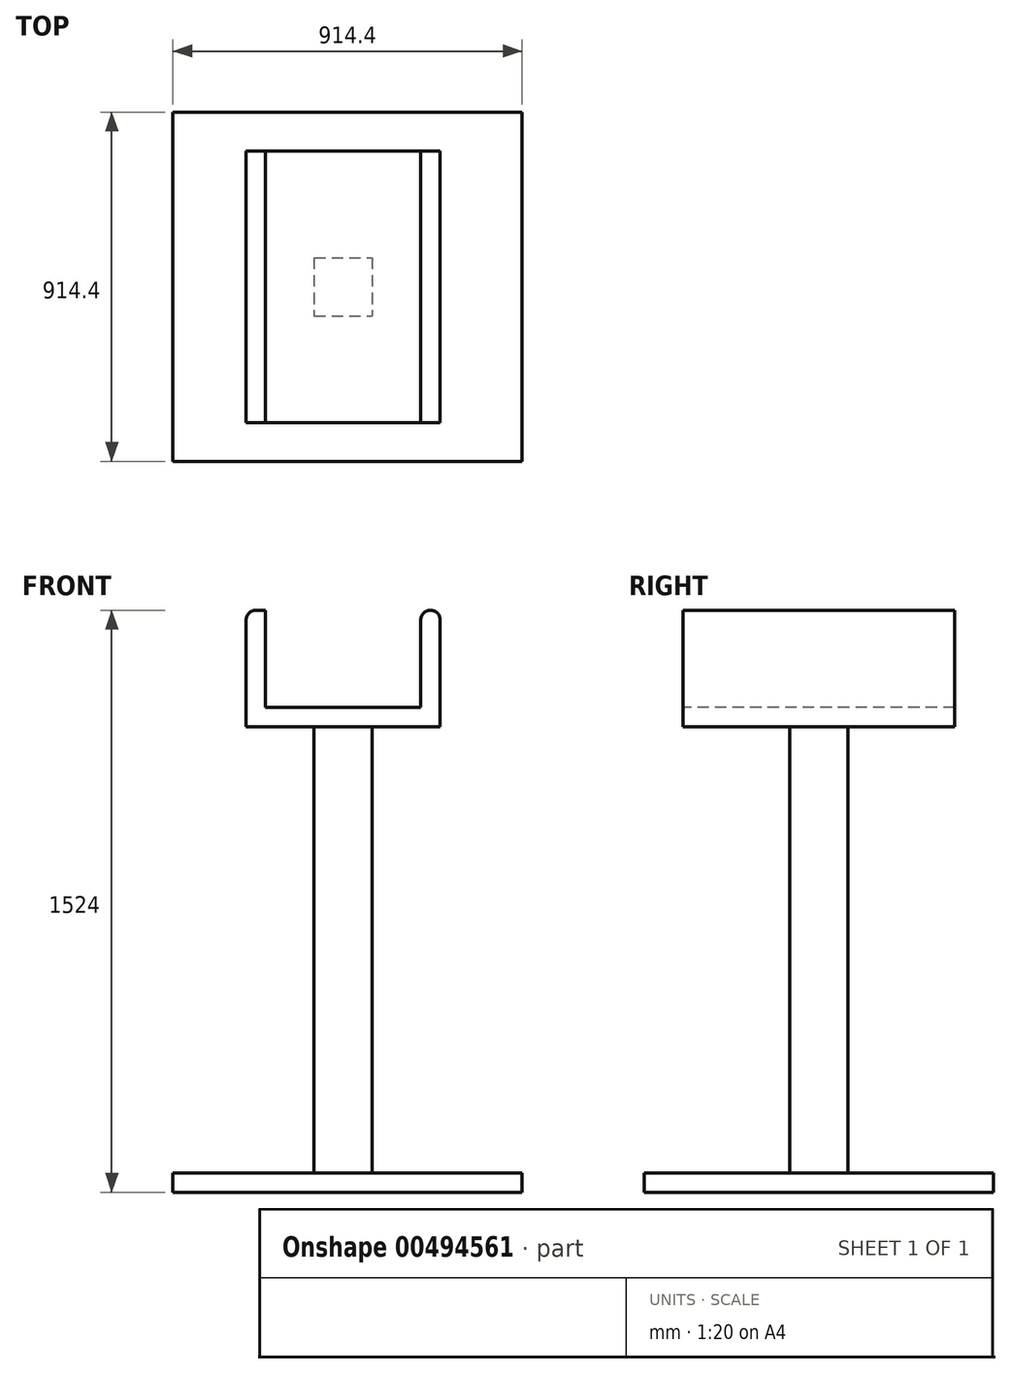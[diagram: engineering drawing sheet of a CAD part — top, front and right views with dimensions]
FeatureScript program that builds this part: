
annotation { "Feature Type Name" : "Feature", "Feature Type Description" : "" }
export const myFeature = defineFeature(function(context is Context, id is Id, definition is map)
    precondition{}
    {
        {
            var Q0;
            Q0=qCreatedBy(makeId("Top.planeOp"),FACE);
            var sketch = newSketch(context, id + "F0", { "sketchPlane" : qUnion([Q0])});
            skLineSegment(sketch, "E0.bottom", {"start": v(-445.84, 457.2) * mm, "end": v(468.56, 457.2) * mm});
            skLineSegment(sketch, "E0.top", {"start": v(-445.84, -457.2) * mm, "end": v(468.56, -457.2) * mm});
            skLineSegment(sketch, "E0.left", {"start": v(-445.84, 457.2) * mm, "end": v(-445.84, -457.2) * mm});
            skLineSegment(sketch, "E0.right", {"start": v(468.56, 457.2) * mm, "end": v(468.56, -457.2) * mm});
            skPoint(sketch, "E0.middle", {"position": v(11.36, 0) * mm});
            skSolve(sketch);
        }
        {
            var Q0;
            Q0=qSketchRegion(id+"F0",true);
            var Q1;
            Q1=qSketchRegion(id+"F2",true);
            extrude(context, id + "F1", {"entities" : qUnion([Q0, Q1]), "depth" : 50.8 * mm, "offsetDistance" : 25.4 * mm});
        }
        {
            var Q0;
            Q0=makeQuery(id+"F1.opExtrude","CAP_FACE",FACE,{"disambiguationData":[OSD([sQuery(id+"F0.wireOp",EDGE,"E0.bottom"),sQuery(id+"F0.wireOp",EDGE,"E0.top"),sQuery(id+"F0.wireOp",EDGE,"E0.left"),sQuery(id+"F0.wireOp",EDGE,"E0.right")])],"isStart":true});
            var sketch = newSketch(context, id + "F2", { "sketchPlane" : qUnion([Q0])});
            skLineSegment(sketch, "E1.bottom", {"start": v(76.2, 76.2) * mm, "end": v(-76.2, 76.2) * mm});
            skLineSegment(sketch, "E1.top", {"start": v(76.2, -76.2) * mm, "end": v(-76.2, -76.2) * mm});
            skLineSegment(sketch, "E1.left", {"start": v(76.2, 76.2) * mm, "end": v(76.2, -76.2) * mm});
            skLineSegment(sketch, "E1.right", {"start": v(-76.2, 76.2) * mm, "end": v(-76.2, -76.2) * mm});
            skPoint(sketch, "E1.middle", {"position": v(0, 0) * mm});
            skSolve(sketch);
        }
        {
            var Q0;
            Q0=qSketchRegion(id+"F2",true);
            extrude(context, id + "F3", {"entities" : qUnion([Q0]), "operationType" : NewBodyOperationType.ADD, "depth" : -1219.2 * mm, "offsetDistance" : 25.4 * mm});
        }
        {
            var Q0;
            Q0=makeQuery(id+"F3.opExtrude","CAP_FACE",FACE,{"disambiguationData":[OSD([sQuery(id+"F2.wireOp",EDGE,"E1.bottom"),sQuery(id+"F2.wireOp",EDGE,"E1.top"),sQuery(id+"F2.wireOp",EDGE,"E1.left"),sQuery(id+"F2.wireOp",EDGE,"E1.right")])],"isStart":false});
            var sketch = newSketch(context, id + "F4", { "sketchPlane" : qUnion([Q0])});
            skLineSegment(sketch, "E2.bottom", {"start": v(-254, 355.6) * mm, "end": v(254, 355.6) * mm});
            skLineSegment(sketch, "E2.top", {"start": v(-254, -355.6) * mm, "end": v(254, -355.6) * mm});
            skLineSegment(sketch, "E2.left", {"start": v(-254, 355.6) * mm, "end": v(-254, -355.6) * mm});
            skLineSegment(sketch, "E2.right", {"start": v(254, 355.6) * mm, "end": v(254, -355.6) * mm});
            skPoint(sketch, "E2.middle", {"position": v(0, 0) * mm});
            skSolve(sketch);
        }
        {
            var Q0;
            Q0=qSketchRegion(id+"F4",true);
            extrude(context, id + "F5", {"entities" : qUnion([Q0]), "operationType" : NewBodyOperationType.ADD, "depth" : 304.8 * mm, "offsetDistance" : 25.4 * mm});
        }
        {
            var Q0;
            Q0=makeQuery(id+"F5.opExtrude","CAP_FACE",FACE,{"disambiguationData":[OSD([sQuery(id+"F4.wireOp",EDGE,"E2.bottom"),sQuery(id+"F4.wireOp",EDGE,"E2.top"),sQuery(id+"F4.wireOp",EDGE,"E2.left"),sQuery(id+"F4.wireOp",EDGE,"E2.right")])],"isStart":false});
            var sketch = newSketch(context, id + "F6", { "sketchPlane" : qUnion([Q0])});
            skLineSegment(sketch, "E3.bottom", {"start": v(203.2, 406.4) * mm, "end": v(-203.2, 406.4) * mm});
            skLineSegment(sketch, "E3.top", {"start": v(203.2, -406.4) * mm, "end": v(-203.2, -406.4) * mm});
            skLineSegment(sketch, "E3.left", {"start": v(203.2, 406.4) * mm, "end": v(203.2, -406.4) * mm});
            skLineSegment(sketch, "E3.right", {"start": v(-203.2, 406.4) * mm, "end": v(-203.2, -406.4) * mm});
            skPoint(sketch, "E3.middle", {"position": v(0, 0) * mm});
            skSolve(sketch);
        }
        {
            var Q0;
            Q0=qSketchRegion(id+"F6",true);
            extrude(context, id + "F7", {"entities" : qUnion([Q0]), "operationType" : NewBodyOperationType.REMOVE, "oppositeDirection" : true, "depth" : 254 * mm, "offsetDistance" : 25.4 * mm});
        }
        {
            var Q0;
            Q0=makeQuery(id+"F5.opExtrude","CAP_EDGE",EDGE,{"disambiguationData":[OSD([sQuery(id+"F4.wireOp",EDGE,"E2.left")])],"isStart":false});
            var Q1;
            Q1=makeQuery(id+"F7.boolean.opBoolean","COPY",EDGE,{"derivedFrom":makeQuery(id+"F7.opExtrude","CAP_EDGE",EDGE,{"disambiguationData":[OSD([sQuery(id+"F6.wireOp",EDGE,"E3.right")])],"isStart":true})});
            var Q2;
            Q2=makeQuery(id+"F7.boolean.opBoolean","COPY",EDGE,{"derivedFrom":makeQuery(id+"F7.opExtrude","CAP_EDGE",EDGE,{"disambiguationData":[OSD([sQuery(id+"F6.wireOp",EDGE,"E3.left")])],"isStart":true})});
            var Q3;
            Q3=makeQuery(id+"F5.opExtrude","CAP_EDGE",EDGE,{"disambiguationData":[OSD([sQuery(id+"F4.wireOp",EDGE,"E2.right")])],"isStart":false});
            fillet(context, id + "F8", {"entities" : qUnion([Q0, Q1, Q2, Q3]), "radius" : 25.4 * mm, "tangentPropagation" : true, "allowEdgeOverflow" : false});
        }
    });
